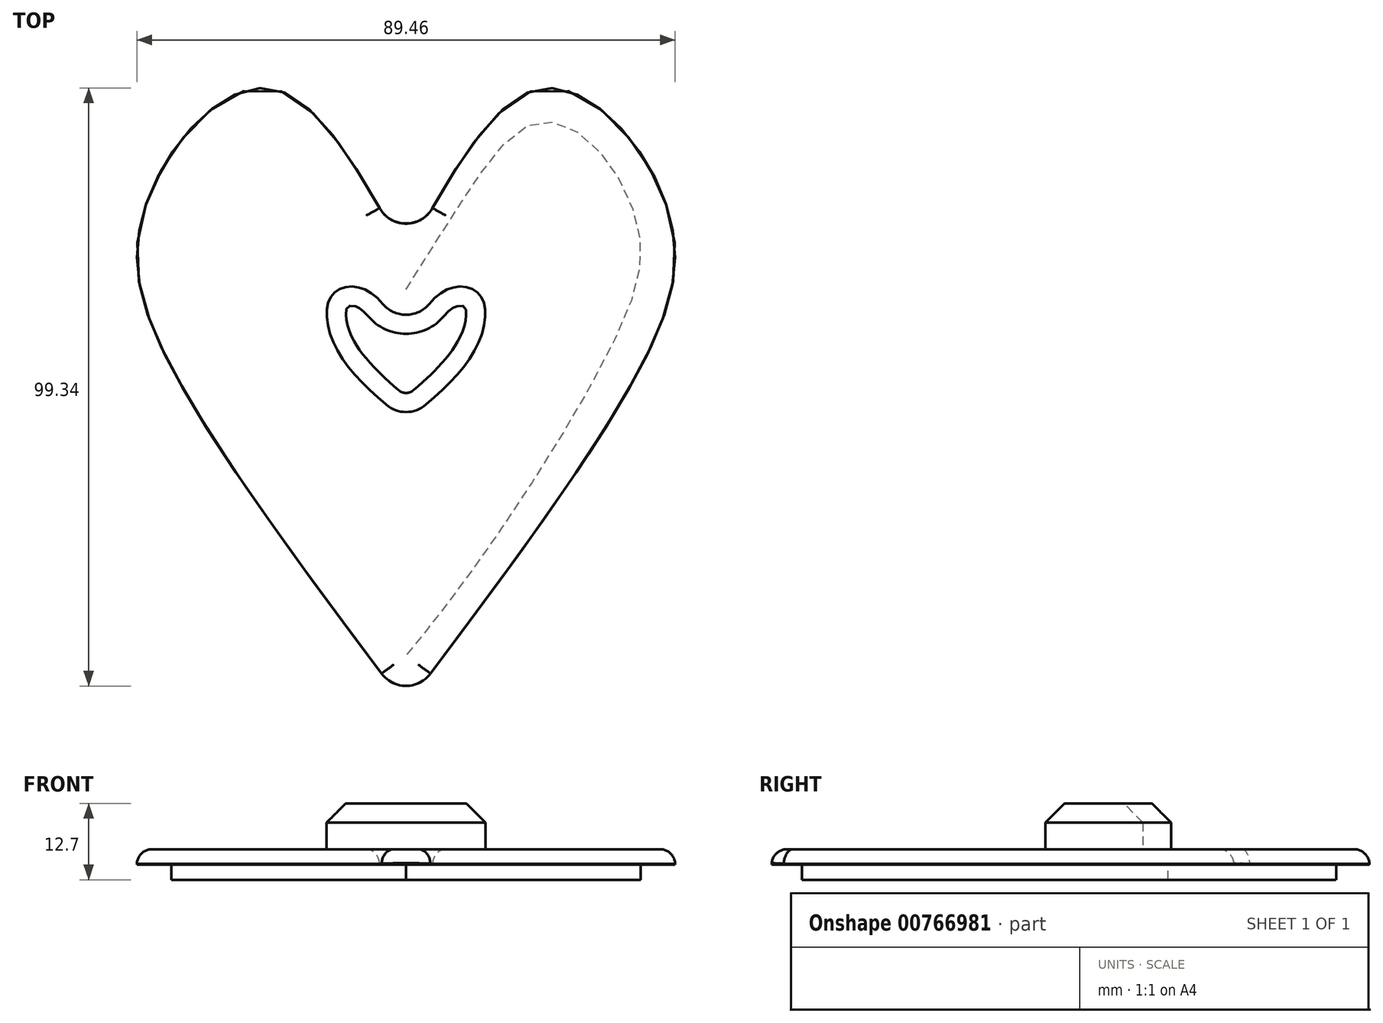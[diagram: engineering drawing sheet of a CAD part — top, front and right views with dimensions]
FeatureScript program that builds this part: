
annotation { "Feature Type Name" : "Feature", "Feature Type Description" : "" }
export const myFeature = defineFeature(function(context is Context, id is Id, definition is map)
    precondition{}
    {
        {
            var Q0;
            Q0=qCreatedBy(makeId("Top.planeOp"),FACE);
            var sketch = newSketch(context, id + "F0", { "sketchPlane" : qUnion([Q0])});
            skLineSegment(sketch, "E0", {"start": v(0, 27.2) * mm, "end": v(0, -47.1) * mm});
            skFitSpline(sketch, "E1", {"points": [v(0, 27.2) * mm, v(21.09, 54.83) * mm, v(34.75, 49.5) * mm, v(43.96, 32.9) * mm, v(41.1, 13.62) * mm, v(0, -47.1) * mm], "startDerivative": vector(94.88, 174.06) * mm, "endDerivative": vector(-162.83, -216.8) * mm});
            skFitSpline(sketch, "E2.MirrorCS", {"points": [v(0, 27.2) * mm, v(-21.09, 54.83) * mm, v(-34.75, 49.5) * mm, v(-43.96, 32.9) * mm, v(-41.1, 13.62) * mm, v(0, -47.1) * mm], "startDerivative": vector(-94.88, 174.06) * mm, "endDerivative": vector(162.83, -216.8) * mm});
            skFitSpline(sketch, "E3", {"points": [v(0, 21.95) * mm, v(9.98, 37.58) * mm, v(21.09, 49.5) * mm, v(30.73, 46.28) * mm, v(38.48, 32.54) * mm, v(36.21, 16.98) * mm, v(13.78, -20.8) * mm, v(0, -38.92) * mm], "startDerivative": vector(68.83, 109.37) * mm, "endDerivative": vector(-80.38, -99.49) * mm});
            skFitSpline(sketch, "E4.MirrorCS", {"points": [v(0, 21.95) * mm, v(-9.98, 37.58) * mm, v(-21.09, 49.5) * mm, v(-30.73, 46.28) * mm, v(-38.48, 32.54) * mm, v(-36.21, 16.98) * mm, v(-13.78, -20.8) * mm, v(0, -38.92) * mm], "startDerivative": vector(-68.83, 109.37) * mm, "endDerivative": vector(80.38, -99.49) * mm});
            skSolve(sketch);
        }
        {
            var Q0;
            {var subQ1=sQuery(id+"F0.wireOp",EDGE,"E1");Q0=makeQuery(id+"F0.imprint","IMPRINT",FACE,{"disambiguationData":[TD([[makeQuery(id+"F0.imprint","IMPRINT",EDGE,{"derivedFrom":subQ1}),-1.0]])]});}
            var Q1;
            {var subQ0=sQuery(id+"F0.wireOp",EDGE,"E2.MirrorCS");Q1=makeQuery(id+"F0.imprint","IMPRINT",FACE,{"disambiguationData":[TD([[makeQuery(id+"F0.imprint","IMPRINT",EDGE,{"derivedFrom":subQ0}),1.0]])]});}
            extrude(context, id + "F1", {"entities" : qUnion([Q0, Q1]), "oppositeDirection" : true, "depth" : 2.54 * mm, "offsetDistance" : 25.4 * mm, "hasDraft" : true, "draftAngle" : 3 * degree});
        }
        {
            var Q0;
            {var subQ1=sQuery(id+"F0.wireOp",EDGE,"E3");Q0=makeQuery(id+"F0.imprint","IMPRINT",FACE,{"disambiguationData":[TD([[makeQuery(id+"F0.imprint","IMPRINT",EDGE,{"derivedFrom":subQ1}),-1.0]])]});}
            var Q1;
            {var subQ0=sQuery(id+"F0.wireOp",EDGE,"E4.MirrorCS");Q1=makeQuery(id+"F0.imprint","IMPRINT",FACE,{"disambiguationData":[TD([[makeQuery(id+"F0.imprint","IMPRINT",EDGE,{"derivedFrom":subQ0}),1.0]])]});}
            extrude(context, id + "F2", {"entities" : qUnion([Q0, Q1]), "operationType" : NewBodyOperationType.ADD, "oppositeDirection" : true, "depth" : 5.08 * mm, "offsetDistance" : 25.4 * mm});
        }
        {
            var Q0;
            {var subQ1=sQuery(id+"F0.wireOp",EDGE,"E3");Q0=makeQuery(id+"F0.imprint","IMPRINT",FACE,{"disambiguationData":[TD([[makeQuery(id+"F0.imprint","IMPRINT",EDGE,{"derivedFrom":subQ1}),-1.0]])]});}
            var sketch = newSketch(context, id + "F3", { "sketchPlane" : qUnion([Q0])});
            skFitSpline(sketch, "E5", {"points": [v(0, 13.56) * mm, v(6.88, 21.95) * mm, v(12.3, 20.99) * mm, v(11.7, 12.34) * mm, v(0, 0) * mm], "startDerivative": vector(23.89, 41.58) * mm, "endDerivative": vector(-43.45, -36.04) * mm});
            skLineSegment(sketch, "E6", {"start": v(0, 13.56) * mm, "end": v(0, 0) * mm});
            skFitSpline(sketch, "E7.MirrorCS", {"points": [v(0, 13.56) * mm, v(-6.88, 21.95) * mm, v(-12.3, 20.99) * mm, v(-11.7, 12.34) * mm, v(0, 0) * mm], "startDerivative": vector(-23.89, 41.58) * mm, "endDerivative": vector(43.45, -36.04) * mm});
            skSolve(sketch);
        }
        {
            var Q0;
            Q0=makeQuery(id+"F3.imprint","IMPRINT",FACE,{"disambiguationData":[TD([[makeQuery(id+"F3.imprint","IMPRINT",EDGE,{"derivedFrom":sQuery(id+"F3.wireOp",EDGE,"E6")}),-1.0]])]});
            var Q1;
            Q1=makeQuery(id+"F3.imprint","IMPRINT",FACE,{"disambiguationData":[TD([[makeQuery(id+"F3.imprint","IMPRINT",EDGE,{"derivedFrom":sQuery(id+"F3.wireOp",EDGE,"E5")}),-1.0]])]});
            extrude(context, id + "F4", {"entities" : qUnion([Q0, Q1]), "operationType" : NewBodyOperationType.ADD, "depth" : 7.62 * mm, "offsetDistance" : 25.4 * mm});
        }
        {
            var Q0;
            {var subQ0=sQuery(id+"F0.wireOp",EDGE,"E2.MirrorCS");var subQ1=sQuery(id+"F0.wireOp",EDGE,"E1");var subQ2=sQuery(id+"F0.wireOp",EDGE,"E0");Q0=makeQuery(id+"F1.opExtrude","SWEPT_EDGE",EDGE,{"disambiguationData":[OSD([subQ2,subQ1,subQ0]),TDD([makeQuery(id+"F0.imprint","INTERSECT",VERTEX,{"disambiguationData":[OD(1.0)],"derivedFrom":[subQ2,subQ1,subQ0]})])]});}
            var Q1;
            {var subQ0=sQuery(id+"F0.wireOp",EDGE,"E2.MirrorCS");var subQ1=sQuery(id+"F0.wireOp",EDGE,"E1");var subQ2=sQuery(id+"F0.wireOp",EDGE,"E0");Q1=makeQuery(id+"F1.opExtrude","SWEPT_EDGE",EDGE,{"disambiguationData":[OSD([subQ2,subQ1,subQ0]),TDD([makeQuery(id+"F0.imprint","INTERSECT",VERTEX,{"disambiguationData":[OD(0.0)],"derivedFrom":[subQ2,subQ1,subQ0]})])]});}
            fillet(context, id + "F5", {"entities" : qUnion([Q0, Q1]), "radius" : 5.08 * mm, "tangentPropagation" : true, "allowEdgeOverflow" : false});
        }
        {
            var Q0;
            Q0=makeQuery(id+"F1.opExtrude","CAP_EDGE",EDGE,{"disambiguationData":[OSD([sQuery(id+"F0.wireOp",EDGE,"E2.MirrorCS")])],"isStart":true});
            fillet(context, id + "F6", {"entities" : qUnion([Q0]), "radius" : 2.54 * mm, "tangentPropagation" : true, "allowEdgeOverflow" : false});
        }
        {
            var Q0;
            {var subQ0=sQuery(id+"F3.wireOp",EDGE,"E7.MirrorCS");var subQ1=sQuery(id+"F3.wireOp",EDGE,"E6");var subQ2=sQuery(id+"F3.wireOp",EDGE,"E5");var subQ3=sQuery(id+"F0.wireOp",EDGE,"E4.MirrorCS");var subQ4=sQuery(id+"F0.wireOp",EDGE,"E3");var subQ5=sQuery(id+"F0.wireOp",EDGE,"E0");Q0=makeQuery(id+"F4.opExtrude","SWEPT_EDGE",EDGE,{"disambiguationData":[OSD([subQ5,subQ2,subQ1,subQ0]),TDD([makeQuery(id+"F3.imprint","INTERSECT",VERTEX,{"disambiguationData":[OD(1.0)],"derivedFrom":[makeQuery(id+"F0.imprint","IMPRINT",EDGE,{"disambiguationData":[TD([[makeQuery(id+"F0.imprint","INTERSECT",VERTEX,{"disambiguationData":[OD(0.0)],"derivedFrom":[subQ5,subQ4,subQ3]}),-1.0]])],"derivedFrom":subQ5}),subQ2,subQ1,subQ0]})])]});}
            var Q1;
            {var subQ0=sQuery(id+"F3.wireOp",EDGE,"E7.MirrorCS");var subQ1=sQuery(id+"F3.wireOp",EDGE,"E6");var subQ2=sQuery(id+"F3.wireOp",EDGE,"E5");var subQ3=sQuery(id+"F0.wireOp",EDGE,"E4.MirrorCS");var subQ4=sQuery(id+"F0.wireOp",EDGE,"E3");var subQ5=sQuery(id+"F0.wireOp",EDGE,"E0");Q1=makeQuery(id+"F4.opExtrude","SWEPT_EDGE",EDGE,{"disambiguationData":[OSD([subQ5,subQ2,subQ1,subQ0]),TDD([makeQuery(id+"F3.imprint","INTERSECT",VERTEX,{"disambiguationData":[OD(0.0)],"derivedFrom":[makeQuery(id+"F0.imprint","IMPRINT",EDGE,{"disambiguationData":[TD([[makeQuery(id+"F0.imprint","INTERSECT",VERTEX,{"disambiguationData":[OD(0.0)],"derivedFrom":[subQ5,subQ4,subQ3]}),-1.0]])],"derivedFrom":subQ5}),subQ2,subQ1,subQ0]})])]});}
            fillet(context, id + "F7", {"entities" : qUnion([Q0, Q1]), "radius" : 5.08 * mm, "tangentPropagation" : true, "allowEdgeOverflow" : false});
        }
        {
            var Q0;
            Q0=makeQuery(id+"F4.opExtrude","CAP_EDGE",EDGE,{"disambiguationData":[OSD([sQuery(id+"F3.wireOp",EDGE,"E7.MirrorCS")])],"isStart":false});
            var Q1;
            Q1=makeQuery(id+"F4.opExtrude","CAP_EDGE",EDGE,{"disambiguationData":[OSD([sQuery(id+"F3.wireOp",EDGE,"E5")])],"isStart":false});
            var Q2;
            {var subQ0=sQuery(id+"F3.wireOp",EDGE,"E7.MirrorCS");var subQ1=sQuery(id+"F3.wireOp",EDGE,"E5");var subQ2=sQuery(id+"F3.wireOp",EDGE,"E6");var subQ3=sQuery(id+"F0.wireOp",EDGE,"E4.MirrorCS");var subQ4=sQuery(id+"F0.wireOp",EDGE,"E3");var subQ5=sQuery(id+"F0.wireOp",EDGE,"E0");Q2=makeQuery(id+"F7.opFillet","BLEND_EDGE",EDGE,{"blendedFrom":[makeQuery(id+"F4.opExtrude","SWEPT_EDGE",EDGE,{"disambiguationData":[OSD([subQ5,subQ1,subQ2,subQ0]),TDD([makeQuery(id+"F3.imprint","INTERSECT",VERTEX,{"disambiguationData":[OD(0.0)],"derivedFrom":[makeQuery(id+"F0.imprint","IMPRINT",EDGE,{"disambiguationData":[TD([[makeQuery(id+"F0.imprint","INTERSECT",VERTEX,{"disambiguationData":[OD(0.0)],"derivedFrom":[subQ5,subQ4,subQ3]}),-1.0]])],"derivedFrom":subQ5}),subQ1,subQ2,subQ0]})])]}),makeQuery(id+"F4.opExtrude","CAP_FACE",FACE,{"disambiguationData":[OSD([subQ1,subQ0])],"isStart":false})],"blendedInto":[makeQuery(id+"F4.opExtrude","CAP_FACE",FACE,{"disambiguationData":[OSD([subQ1,subQ0])],"isStart":false})]});}
            chamfer(context, id + "F8", {"entities" : qUnion([Q0, Q1, Q2]), "width" : 3.17 * mm, "tangentPropagation" : true});
        }
    });
